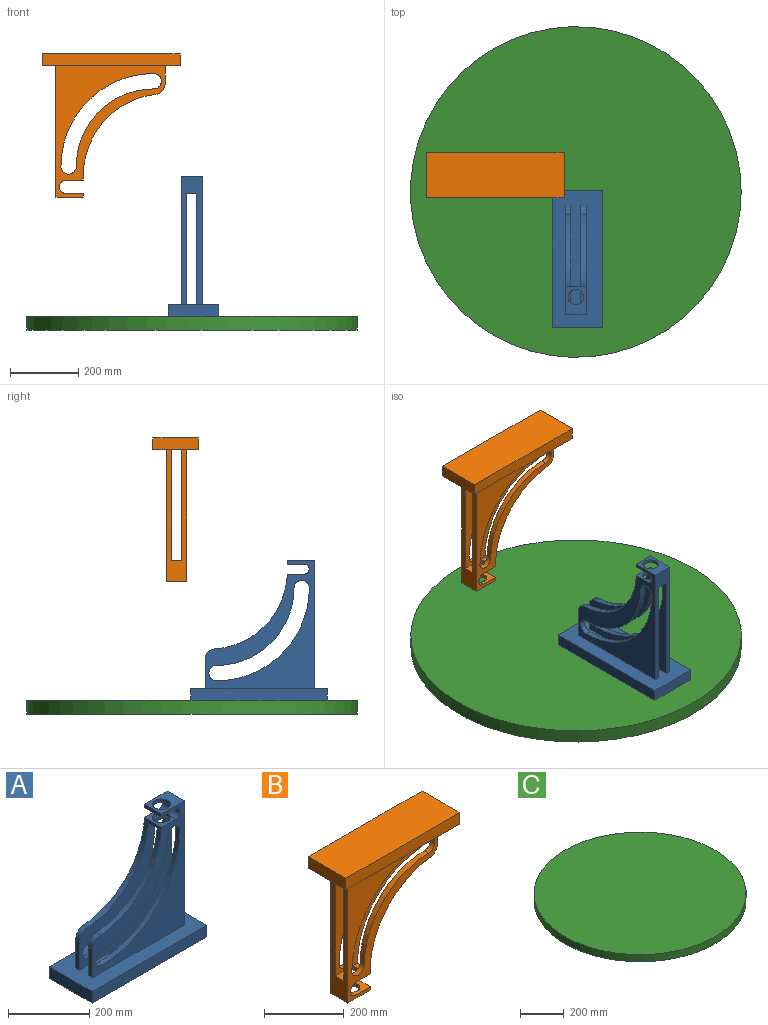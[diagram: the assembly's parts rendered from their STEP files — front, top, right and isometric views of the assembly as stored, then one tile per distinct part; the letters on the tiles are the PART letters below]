
ASSEMBLY  parts=3 mates=3
PART A: 37 faces, bbox 399.7x149.2x410 mm
  f0: plane 30x13.23mm, normal (0,0,-1), area 279mm2, adj f7,f9,f28,f35
  f1: plane 33.23x30mm, normal (0,0,-1), area 879mm2, adj f6,f7,f9,f35
  f2: plane 60x10mm, normal (-1,0,0), area 600mm2, adj f3,f8,f29,f32
  f3: plane 375x320mm, normal (0,-1,0), area 47401mm2, adj f2,f5,f6,f14,f20,f21,f22,f23
  f4: plane 86.04x15mm, normal (-1,0,0), area 1290.6mm2, adj f8,f9,f14,f26
  f5: plane 86.04x15mm, normal (-1,0,0), area 1290.6mm2, adj f3,f7,f14,f27
  f6: plane 375x60mm, normal (1,0,0), area 12750mm2, adj f1,f3,f7,f8,f9,f14,f29
  f7: plane 325x320mm, normal (0,1,0), area 45254.4mm2, adj f0,f1,f5,f6,f14,f20,f21,f22
  f8: plane 375x320mm, normal (0,1,0), area 47401mm2, adj f2,f4,f6,f14,f16,f17,f18,f19
  f9: plane 325x320mm, normal (0,-1,0), area 45254.4mm2, adj f0,f1,f4,f6,f14,f16,f17,f18
  f10: plane 149.23x35mm, normal (-1,0,0), area 5223mm2, adj f11,f13,f14,f15
  f11: plane 399.74x35mm, normal (0,1,0), area 13990.8mm2, adj f10,f12,f14,f15
  f12: plane 149.23x35mm, normal (1,0,0), area 5223mm2, adj f11,f13,f14,f15
  f13: plane 399.74x35mm, normal (0,-1,0), area 13990.8mm2, adj f10,f12,f14,f15
  f14: plane 399.74x149.23mm, normal (0,0,1), area 50052.1mm2, adj f3,f4,f5,f6,f7,f8,f9,f10
  f15: plane 399.74x149.23mm, normal (0,0,-1), area 59652.1mm2, adj f10,f11,f12,f13
  f16: cylinder r=227.5mm len=227.5mm, axis (0,-1,0), area 5360.3mm2, adj f8,f9,f17,f19
  f17: cylinder r=22.5mm len=45mm, axis (0,-1,0), area 1060.3mm2, adj f8,f9,f16,f18
  f18: cylinder r=272.5mm len=272.5mm, axis (0,-1,0), area 6420.6mm2, adj f8,f9,f17,f19
  f19: cylinder r=22.5mm len=45mm, axis (0,-1,0), area 1060.3mm2, adj f8,f9,f16,f18
  f20: cylinder r=22.5mm len=45mm, axis (0,-1,0), area 1060.3mm2, adj f3,f7,f21,f23
  f21: cylinder r=272.5mm len=272.5mm, axis (0,-1,0), area 6420.6mm2, adj f3,f7,f20,f22
  f22: cylinder r=22.5mm len=45mm, axis (0,-1,0), area 1060.3mm2, adj f3,f7,f21,f23
  f23: cylinder r=227.5mm len=227.5mm, axis (0,-1,0), area 5360.3mm2, adj f3,f7,f20,f22
  f24: cylinder r=227.86mm len=211.99mm, axis (0,1,0), area 4866.4mm2, adj f8,f9,f26,f28
  f25: cylinder r=227.86mm len=211.99mm, axis (0,1,0), area 4866.4mm2, adj f3,f7,f27,f28
  f26: cylinder r=30mm len=29.93mm, axis (0,1,0), area 677mm2, adj f4,f8,f9,f24
  f27: cylinder r=30mm len=29.93mm, axis (0,1,0), area 677mm2, adj f3,f5,f7,f25
  f28: plane 60x10mm, normal (-1,0,0), area 600mm2, adj f0,f3,f8,f24,f25,f30
  f29: plane 80x60mm, normal (0,0,1), area 3209.6mm2, adj f2,f3,f6,f8,f33
  f30: plane 60x50mm, normal (0,0,1), area 1444.3mm2, adj f3,f8,f28,f31,f35
  f31: cylinder r=15mm len=60mm, axis (0,-1,0), area 2757.7mm2, adj f3,f8,f30,f32,f33,f35
  f32: plane 60x50mm, normal (0,0,-1), area 1444.3mm2, adj f2,f3,f8,f31,f33
  f33: cylinder r=22.5mm len=45mm, axis (0,0,1), area 1416.1mm2, adj f29,f31,f32
  f34: plane 33.54x7.5mm, normal (0,0,1), area 174.2mm2, adj f9,f35
  f35: cylinder r=22.5mm len=45mm, axis (0,0,1), area 1416.1mm2, adj f0,f1,f30,f31,f34,f36
  f36: plane 33.54x7.5mm, normal (0,0,1), area 174.2mm2, adj f7,f35
PART B: 37 faces, bbox 403.9x133.2x420 mm
  f0: plane 30x21.77mm, normal (0,0,1), area 512.3mm2, adj f2,f5,f6,f34
  f1: plane 31.77x30mm, normal (0,0,1), area 812.3mm2, adj f5,f6,f9,f34
  f2: plane 60x10mm, normal (1,0,0), area 600mm2, adj f0,f3,f4,f24,f25,f31
  f3: plane 385x320mm, normal (0,1,0), area 40748.7mm2, adj f2,f7,f9,f14,f16,f17,f18,f19
  f4: plane 385x320mm, normal (0,-1,0), area 40748.7mm2, adj f2,f8,f9,f14,f20,f21,f22,f23
  f5: plane 325x320mm, normal (0,1,0), area 38577mm2, adj f0,f1,f8,f9,f14,f20,f21,f22
  f6: plane 325x320mm, normal (0,-1,0), area 38577mm2, adj f0,f1,f7,f9,f14,f16,f17,f18
  f7: plane 53.51x15mm, normal (1,0,0), area 802.7mm2, adj f3,f6,f14,f27
  f8: plane 53.51x15mm, normal (1,0,0), area 802.7mm2, adj f4,f5,f14,f26
  f9: plane 385x60mm, normal (-1,0,0), area 13350mm2, adj f1,f3,f4,f5,f6,f14,f29
  f10: plane 133.21x35mm, normal (-1,0,0), area 4662.4mm2, adj f11,f13,f14,f15
  f11: plane 403.91x35mm, normal (0,-1,0), area 14136.9mm2, adj f10,f12,f14,f15
  f12: plane 133.21x35mm, normal (1,0,0), area 4662.4mm2, adj f11,f13,f14,f15
  f13: plane 403.91x35mm, normal (0,1,0), area 14136.9mm2, adj f10,f12,f14,f15
  f14: plane 403.91x133.21mm, normal (0,0,-1), area 44205.5mm2, adj f3,f4,f5,f6,f7,f8,f9,f10
  f15: plane 403.91x133.21mm, normal (0,0,1), area 53805.5mm2, adj f10,f11,f12,f13
  f16: cylinder r=22.5mm len=45mm, axis (0,-1,0), area 1060.3mm2, adj f3,f6,f17,f19
  f17: cylinder r=272.5mm len=272.5mm, axis (0,-1,0), area 6420.6mm2, adj f3,f6,f16,f18
  f18: cylinder r=22.5mm len=45mm, axis (0,-1,0), area 1060.3mm2, adj f3,f6,f17,f19
  f19: cylinder r=227.5mm len=227.5mm, axis (0,-1,0), area 5360.3mm2, adj f3,f6,f16,f18
  f20: cylinder r=227.5mm len=227.5mm, axis (0,-1,0), area 5360.3mm2, adj f4,f5,f21,f23
  f21: cylinder r=22.5mm len=45mm, axis (0,-1,0), area 1060.3mm2, adj f4,f5,f20,f22
  f22: cylinder r=272.5mm len=272.5mm, axis (0,-1,0), area 6420.6mm2, adj f4,f5,f21,f23
  f23: cylinder r=22.5mm len=45mm, axis (0,-1,0), area 1060.3mm2, adj f4,f5,f20,f22
  f24: cylinder r=240.02mm len=241.67mm, axis (0,-1,0), area 5301.6mm2, adj f2,f3,f6,f27
  f25: cylinder r=240.02mm len=241.67mm, axis (0,-1,0), area 5301.6mm2, adj f2,f4,f5,f26
  f26: cylinder r=30mm len=29.81mm, axis (0,-1,0), area 656.8mm2, adj f4,f5,f8,f25
  f27: cylinder r=30mm len=29.81mm, axis (0,-1,0), area 656.8mm2, adj f3,f6,f7,f24
  f28: plane 60x10mm, normal (1,0,0), area 600mm2, adj f3,f4,f29,f30
  f29: plane 80x60mm, normal (0,0,-1), area 3543.4mm2, adj f3,f4,f9,f28,f36
  f30: plane 60x50mm, normal (0,0,1), area 1834mm2, adj f3,f4,f28,f32,f36
  f31: plane 60x50mm, normal (0,0,-1), area 1834mm2, adj f2,f3,f4,f32,f34
  f32: cylinder r=20mm len=60mm, axis (0,-1,0), area 3587.2mm2, adj f3,f4,f30,f31,f34,f36
  f33: plane 26.46x5mm, normal (0,0,-1), area 90.7mm2, adj f6,f34
  f34: cylinder r=20mm len=40mm, axis (0,0,-1), area 1266.3mm2, adj f0,f1,f31,f32,f33,f35
  f35: plane 26.46x5mm, normal (0,0,-1), area 90.7mm2, adj f5,f34
  f36: cylinder r=20mm len=40mm, axis (0,0,-1), area 1266.3mm2, adj f29,f30,f32
PART C: 3 faces, bbox 970x970x40 mm
  f0: cylinder r=485mm len=970mm, axis (0,0,-1), area 121893.8mm2, adj f1,f2
  f1: plane 970x970mm, normal (0,0,1), area 738981.1mm2, adj f0
  f2: plane 970x970mm, normal (0,0,-1), area 738981.1mm2, adj f0
PLACE A rot(axis=(0,0,-1),90deg) t=(71.07,-358.78,0)mm
PLACE B rot(axis=(0,0,-1),0deg) t=(-78.55,50.05,410)mm
PLACE C rot(axis=(0,0,1),0deg) t=(0,0,-40)mm
MATE parallel B.f31 <-> A.f32  axis (0,0,-1) through (-338.04,44.78,400)mm
MATE slider B.f34 <-> A.f29  axis (0,0,1) through (-353.55,44.78,360)mm
MATE planar A.f15 <-> C.f0  axis (0,0,-1) through (-69.94,-196.72,0)mm
